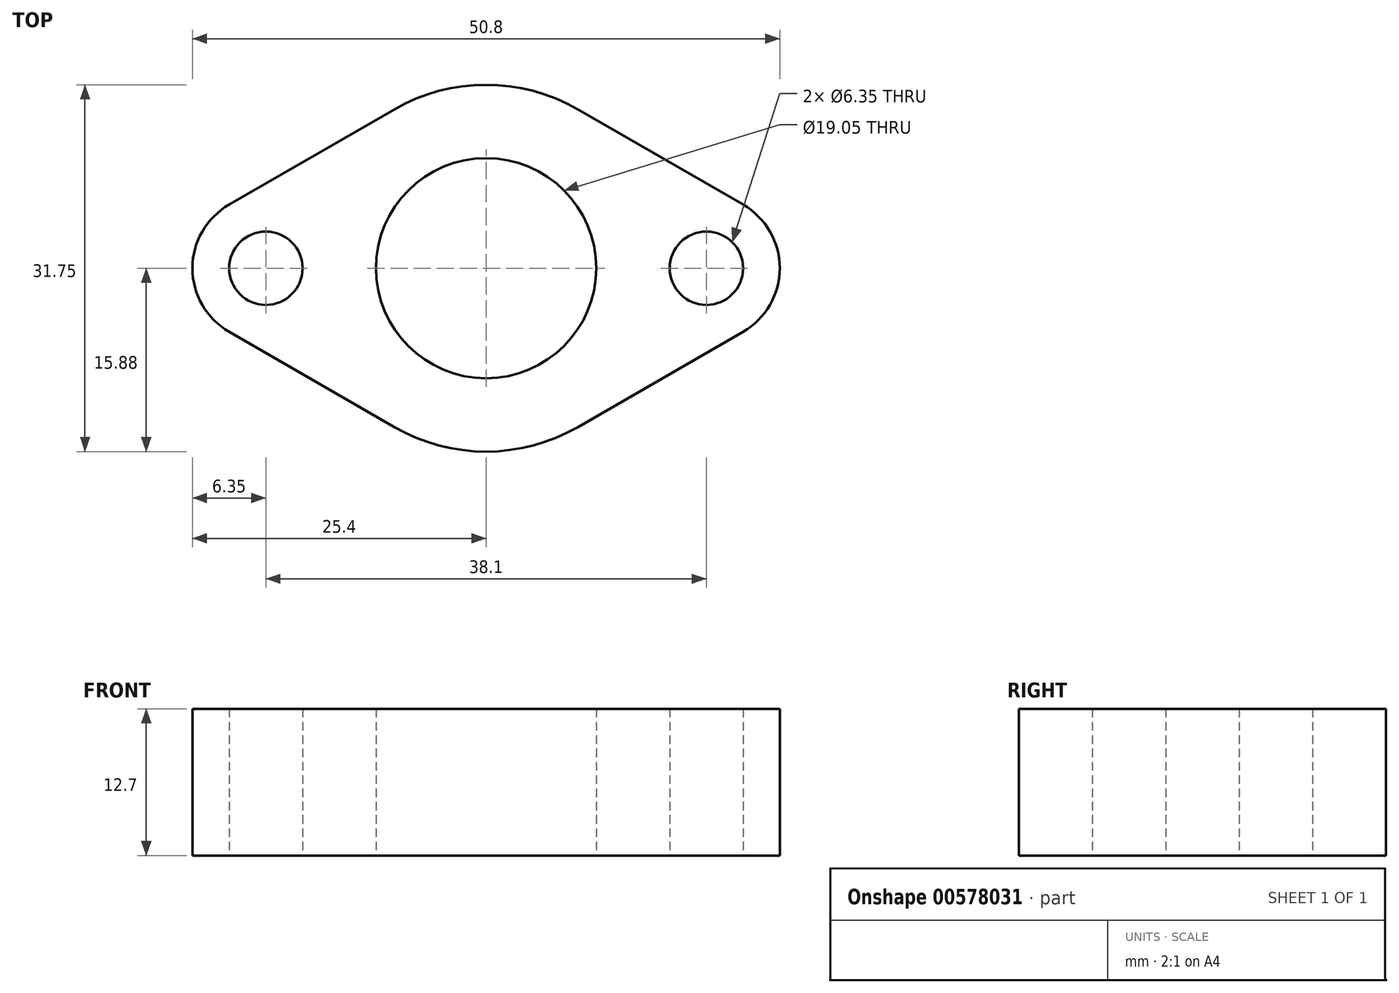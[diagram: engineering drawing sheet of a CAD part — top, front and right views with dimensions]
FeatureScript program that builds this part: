
annotation { "Feature Type Name" : "Feature", "Feature Type Description" : "" }
export const myFeature = defineFeature(function(context is Context, id is Id, definition is map)
    precondition{}
    {
        {
            var Q0;
            Q0=qCreatedBy(makeId("Top.planeOp"),FACE);
            var sketch = newSketch(context, id + "F0", { "sketchPlane" : qUnion([Q0])});
            skCircle(sketch, "E0", {"center": v(0, 0) * mm, "radius": 9.53 * mm});
            skCircle(sketch, "E1", {"center": v(-19.05, 0) * mm, "radius": 3.18 * mm});
            skCircle(sketch, "E2", {"center": v(19.05, 0) * mm, "radius": 3.18 * mm});
            skArc(sketch, "E3", {"start": v(22.22, -5.5) * mm, "mid": v(25.4, 0) * mm, "end": v(22.22, 5.5) * mm});
            skArc(sketch, "E4", {"start": v(-7.94, -13.75) * mm, "mid": v(0, -15.88) * mm, "end": v(7.94, -13.75) * mm});
            skArc(sketch, "E5", {"start": v(-22.23, 5.5) * mm, "mid": v(-25.4, 0) * mm, "end": v(-22.23, -5.5) * mm});
            skLineSegment(sketch, "E6", {"start": v(-22.23, 5.5) * mm, "end": v(-7.94, 13.75) * mm});
            skLineSegment(sketch, "E7", {"start": v(-22.23, -5.5) * mm, "end": v(-7.94, -13.75) * mm});
            skLineSegment(sketch, "E8", {"start": v(22.22, 5.5) * mm, "end": v(7.94, 13.75) * mm});
            skLineSegment(sketch, "E9", {"start": v(22.22, -5.5) * mm, "end": v(7.94, -13.75) * mm});
            skArc(sketch, "E10.trimOffspring", {"start": v(7.94, 13.75) * mm, "mid": v(0, 15.88) * mm, "end": v(-7.94, 13.75) * mm});
            skLineSegment(sketch, "E11", {"start": v(-19.05, 0) * mm, "end": v(19.05, 0) * mm});
            skSolve(sketch);
        }
        {
            var Q0;
            Q0=makeQuery(id+"F0.imprint","IMPRINT",FACE,{"disambiguationData":[TD([[makeQuery(id+"F0.imprint","IMPRINT",EDGE,{"derivedFrom":sQuery(id+"F0.wireOp",EDGE,"E1")}),-1.0]])]});
            extrude(context, id + "F1", {"entities" : qUnion([Q0]), "depth" : 12.7 * mm, "offsetDistance" : 25 * mm});
        }
    });
